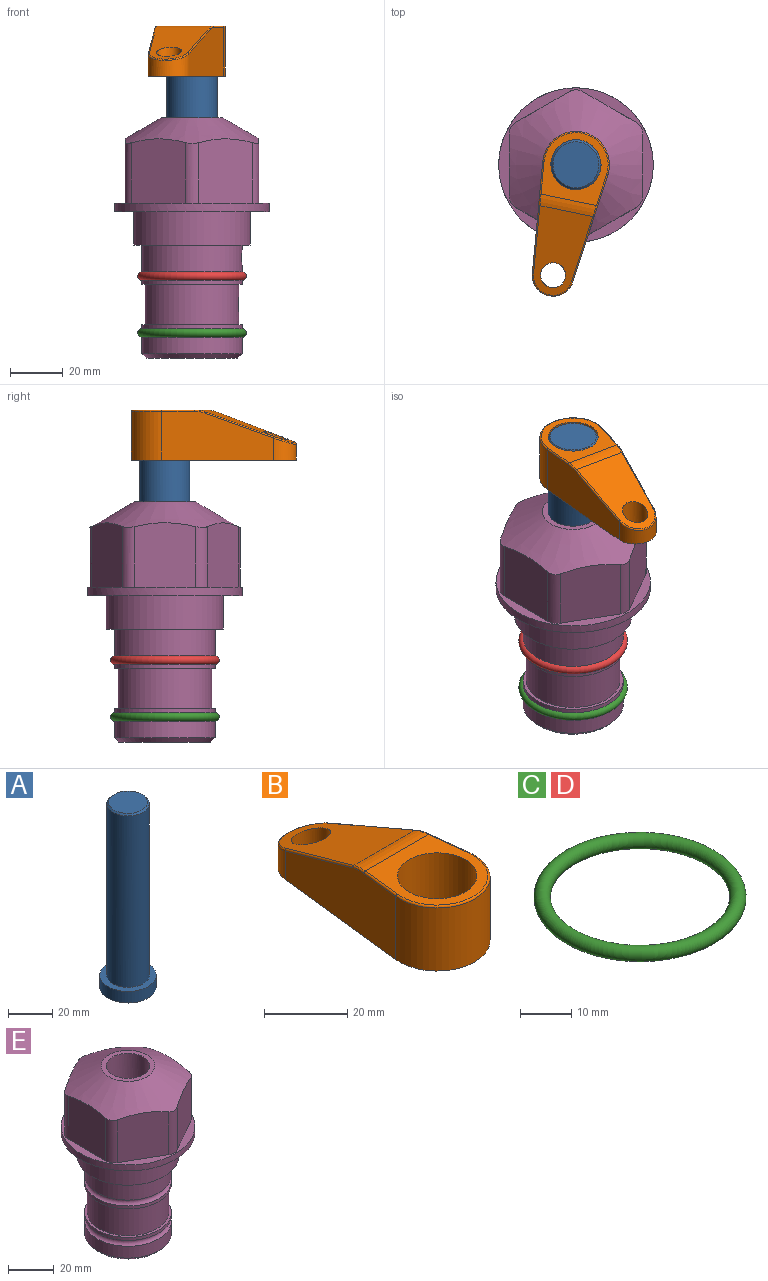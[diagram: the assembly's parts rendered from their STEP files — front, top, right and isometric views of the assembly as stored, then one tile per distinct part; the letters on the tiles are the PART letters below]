
ASSEMBLY  parts=5 mates=3
PART A: 6 faces, bbox 25.4x25.4x101.6 mm
  f0: plane 17.46x17.46mm, normal (0,0,1), area 239.5mm2, adj f5
  f1: plane 25.4x25.4mm, normal (0,0,-1), area 506.7mm2, adj f2
  f2: cylinder r=12.7mm len=25.4mm, axis (0,0,1), area 506.7mm2, adj f1,f3
  f3: plane 25.4x25.4mm, normal (0,0,1), area 221.7mm2, adj f2,f4
  f4: cylinder r=9.53mm len=94.46mm, axis (0,0,1), area 5653mm2, adj f3,f5
  f5: cone r=8.73mm half-angle=45deg, axis (0,0,-1), area 64.4mm2, adj f0,f4
PART B: 44 faces, bbox 27.5x64.5x19.1 mm
  f0: plane 2.3x0.95mm, normal (0,0,-1), area 1mm2, adj f25,f30,f34
  f1: plane 63.5x25.4mm, normal (0,0,-1), area 561.7mm2, adj f2,f3,f4,f5,f6,f7,f19,f20
  f2: cylinder r=12.7mm len=25.4mm, axis (0,0,-1), area 792.2mm2, adj f1,f3,f5,f13
  f3: plane 42.33x18.54mm, normal (0.99,0.11,0), area 647mm2, adj f1,f2,f4,f11,f12,f14
  f4: cylinder r=7.94mm len=15.78mm, axis (0,0,-1), area 158.6mm2, adj f1,f3,f5,f16
  f5: plane 42.33x18.54mm, normal (-0.99,0.11,0), area 647mm2, adj f1,f2,f4,f15,f17,f18
  f6: cylinder r=9.53mm len=19.05mm, axis (0,0,-1), area 1140.1mm2, adj f1,f8
  f7: cylinder r=4.76mm len=10.98mm, axis (0,0,-1), area 276.1mm2, adj f1,f9
  f8: plane 25.83x24.38mm, normal (0,0,1), area 262.2mm2, adj f6,f10,f11,f13,f15
  f9: plane 32.49x20.55mm, normal (0,0.34,0.94), area 489.9mm2, adj f7,f10,f14,f16,f18
  f10: cylinder r=12.7mm len=21.49mm, axis (-1,0,0), area 93.2mm2, adj f8,f9,f12,f17
  f11: cylinder r=0.51mm len=12.34mm, axis (0.11,-0.99,0), area 9.9mm2, adj f3,f8,f12,f13
  f12: bspline ~7.62x1.64mm, area 3.5mm2, adj f3,f10,f11,f14
  f13: torus R=12.19mm, axis (0,0,1), area 33.6mm2, adj f2,f8,f11,f15
  f14: cylinder r=0.51mm len=26.01mm, axis (0.1,-0.93,0.34), area 21.6mm2, adj f3,f9,f12,f16
  f15: cylinder r=0.51mm len=12.34mm, axis (0.11,0.99,0), area 9.9mm2, adj f5,f8,f13,f17
  f16: bspline ~15.78x7.05mm, area 15.7mm2, adj f4,f9,f14,f18
  f17: bspline ~7.62x1.64mm, area 3.5mm2, adj f5,f10,f15,f18
  f18: cylinder r=0.51mm len=26.01mm, axis (0.1,0.93,-0.34), area 21.6mm2, adj f5,f9,f16,f17
  f19: plane 21.6x14.29mm, normal (-0.99,-0.11,0), area 242.6mm2, adj f1,f26,f28,f34,f36,f38
  f20: plane 21.6x14.29mm, normal (0.99,-0.11,0), area 242.6mm2, adj f1,f27,f29,f37,f39,f41
  f21: cylinder r=12.7mm len=14.29mm, axis (0,0,-1), area 173.2mm2, adj f1,f26,f27,f30,f31,f33
  f22: cylinder r=7.94mm len=7.63mm, axis (0,0,-1), area 53.8mm2, adj f1,f28,f29,f42
  f23: plane 2.3x0.95mm, normal (0,0,-1), area 1mm2, adj f25,f33,f37
  f24: plane 17.94x12.32mm, normal (0,-0.34,-0.94), area 191.2mm2, adj f25,f38,f41,f42
  f25: cylinder r=9.53mm len=12.93mm, axis (-1,0,0), area 37.5mm2, adj f0,f23,f24,f31,f36,f39
  f26: cylinder r=1.59mm len=14.29mm, axis (0,0,-1), area 49mm2, adj f1,f19,f21,f32
  f27: cylinder r=1.59mm len=14.29mm, axis (0,0,-1), area 49mm2, adj f1,f20,f21,f35
  f28: cylinder r=1.59mm len=7.28mm, axis (0,0,-1), area 22.1mm2, adj f1,f19,f22,f40
  f29: cylinder r=1.59mm len=7.28mm, axis (0,0,-1), area 22.1mm2, adj f1,f20,f22,f43
  f30: torus R=14.29mm, axis (0,0,1), area 5.8mm2, adj f0,f21,f31,f32
  f31: bspline ~11.06x2.73mm, area 20.8mm2, adj f21,f25,f30,f33
  f32: sphere r=1.59mm, area 5.4mm2, adj f26,f30,f34
  f33: torus R=14.29mm, axis (0,0,1), area 5.8mm2, adj f21,f23,f31,f35
  f34: cylinder r=1.59mm len=1.68mm, axis (-0.11,0.99,0), area 2.4mm2, adj f0,f19,f32,f36
  f35: sphere r=1.59mm, area 5.4mm2, adj f27,f33,f37
  f36: bspline ~5.82x2.33mm, area 7.7mm2, adj f19,f25,f34,f38
  f37: cylinder r=1.59mm len=1.68mm, axis (0.11,0.99,0), area 2.4mm2, adj f20,f23,f35,f39
  f38: cylinder r=1.59mm len=18.33mm, axis (0.1,-0.93,0.34), area 46.7mm2, adj f19,f24,f36,f40
  f39: bspline ~5.82x2.33mm, area 7.7mm2, adj f20,f25,f37,f41
  f40: sphere r=1.59mm, area 3.6mm2, adj f28,f38,f42
  f41: cylinder r=1.59mm len=18.33mm, axis (0.1,0.93,-0.34), area 46.7mm2, adj f20,f24,f39,f43
  f42: bspline ~8.31x1.84mm, area 15.3mm2, adj f22,f24,f40,f43
  f43: sphere r=1.59mm, area 3.6mm2, adj f29,f41,f42
PART C: 1 faces, bbox 44.7x44.7x3.2 mm
  f0: torus R=19.05mm, axis (0,0,1), area 1193.9mm2
PART D: same geometry as C
PART E: 36 faces, bbox 58.7x58.7x91.2 mm
  f0: cylinder r=17.78mm len=35.56mm, axis (0,0,1), area 1670.8mm2, adj f23,f24,f31
  f1: cylinder r=19.05mm len=38.1mm, axis (0,0,1), area 1191.9mm2, adj f26,f27,f30
  f2: plane 58.66x58.66mm, normal (0,0,-1), area 1150.6mm2, adj f3,f28
  f3: cylinder r=29.33mm len=58.66mm, axis (0,0,-1), area 585.1mm2, adj f2,f4
  f4: plane 58.66x58.66mm, normal (0,0,1), area 475.9mm2, adj f3,f5,f6,f7,f8,f9,f10,f11
  f5: plane 24.5x20.32mm, normal (-0.5,0.87,0), area 562.8mm2, adj f4,f15,f16,f17
  f6: plane 24.5x20.32mm, normal (0.5,0.87,0), area 562.8mm2, adj f4,f14,f15,f17
  f7: plane 24.5x23.48mm, normal (1,0,0), area 562.8mm2, adj f4,f13,f14,f17
  f8: plane 24.5x20.32mm, normal (0.5,-0.87,0), area 562.8mm2, adj f4,f12,f13,f17
  f9: plane 24.5x20.32mm, normal (-0.5,-0.87,0), area 562.8mm2, adj f4,f11,f12,f17
  f10: plane 24.5x23.48mm, normal (-1,0,0), area 562.8mm2, adj f4,f11,f16,f17
  f11: cylinder r=5.08mm len=23.01mm, axis (0,0,-1), area 121.2mm2, adj f4,f9,f10,f17
  f12: cylinder r=5.08mm len=23.01mm, axis (0,0,-1), area 121.2mm2, adj f4,f8,f9,f17
  f13: cylinder r=5.08mm len=23.01mm, axis (0,0,-1), area 121.2mm2, adj f4,f7,f8,f17
  f14: cylinder r=5.08mm len=23.01mm, axis (0,0,-1), area 121.2mm2, adj f4,f6,f7,f17
  f15: cylinder r=5.08mm len=23.01mm, axis (0,0,-1), area 121.2mm2, adj f4,f5,f6,f17
  f16: cylinder r=5.08mm len=23.01mm, axis (0,0,-1), area 121.2mm2, adj f4,f5,f10,f17
  f17: cone r=11.73mm half-angle=60deg, axis (0,0,-1), area 2071.8mm2, adj f5,f6,f7,f8,f9,f10,f11,f12
  f18: plane 23.46x23.46mm, normal (0,0,1), area 147.4mm2, adj f17,f35
  f19: plane 34.93x34.93mm, normal (0,0,-1), area 958mm2, adj f29
  f20: cylinder r=19.05mm len=38.1mm, axis (0,0,1), area 760.1mm2, adj f21,f29
  f21: torus R=19.05mm, axis (0,0,1), area 565.3mm2, adj f20,f22
  f22: cylinder r=19.05mm len=38.1mm, axis (0,0,1), area 190mm2, adj f21,f23
  f23: plane 38.1x38.1mm, normal (0,0,1), area 146.9mm2, adj f0,f22
  f24: plane 38.1x38.1mm, normal (0,0,-1), area 146.9mm2, adj f0,f25
  f25: cylinder r=19.05mm len=38.1mm, axis (0,0,1), area 190mm2, adj f24,f26
  f26: torus R=19.05mm, axis (0,0,1), area 565.3mm2, adj f1,f25
  f27: plane 44.45x44.45mm, normal (0,0,-1), area 411.7mm2, adj f1,f28
  f28: cylinder r=22.23mm len=44.45mm, axis (0,0,1), area 1773.5mm2, adj f2,f27
  f29: cone r=19.05mm half-angle=45deg, axis (0,0,1), area 257.5mm2, adj f19,f20
  f30: cylinder r=3.17mm len=6.75mm, axis (-1,0,0), area 128mm2, adj f1,f33
  f31: cylinder r=3.17mm len=6.35mm, axis (-1,0,0), area 102.5mm2, adj f0,f33
  f32: plane 25.4x25.4mm, normal (0,0,1), area 506.7mm2, adj f33
  f33: cylinder r=12.7mm len=66.42mm, axis (0,0,-1), area 5236.2mm2, adj f30,f31,f32,f34
  f34: cone r=9.53mm half-angle=30deg, axis (0,0,-1), area 443.4mm2, adj f33,f35
  f35: cylinder r=9.53mm len=19.05mm, axis (0,0,-1), area 849mm2, adj f18,f34
PLACE A rot(axis=(0,0,-1),101.7deg) t=(0,0,-3.16)mm
PLACE B rot(axis=(0,0,1),168.3deg) t=(0,0,51.45)mm
PLACE C t=(0,0,-21.59)mm
PLACE D at identity
PLACE E at identity fixed
MATE fastened C.f0 <-> E.f0  axis (0,0,1) through (0,0,-46.1)mm
MATE cylindrical A.f2 <-> E.f0  axis (0,0,1) through (0,0,22.48)mm
MATE fastened B.f2 <-> A.f2  axis (0,0,1) through (0,0,70.5)mm
